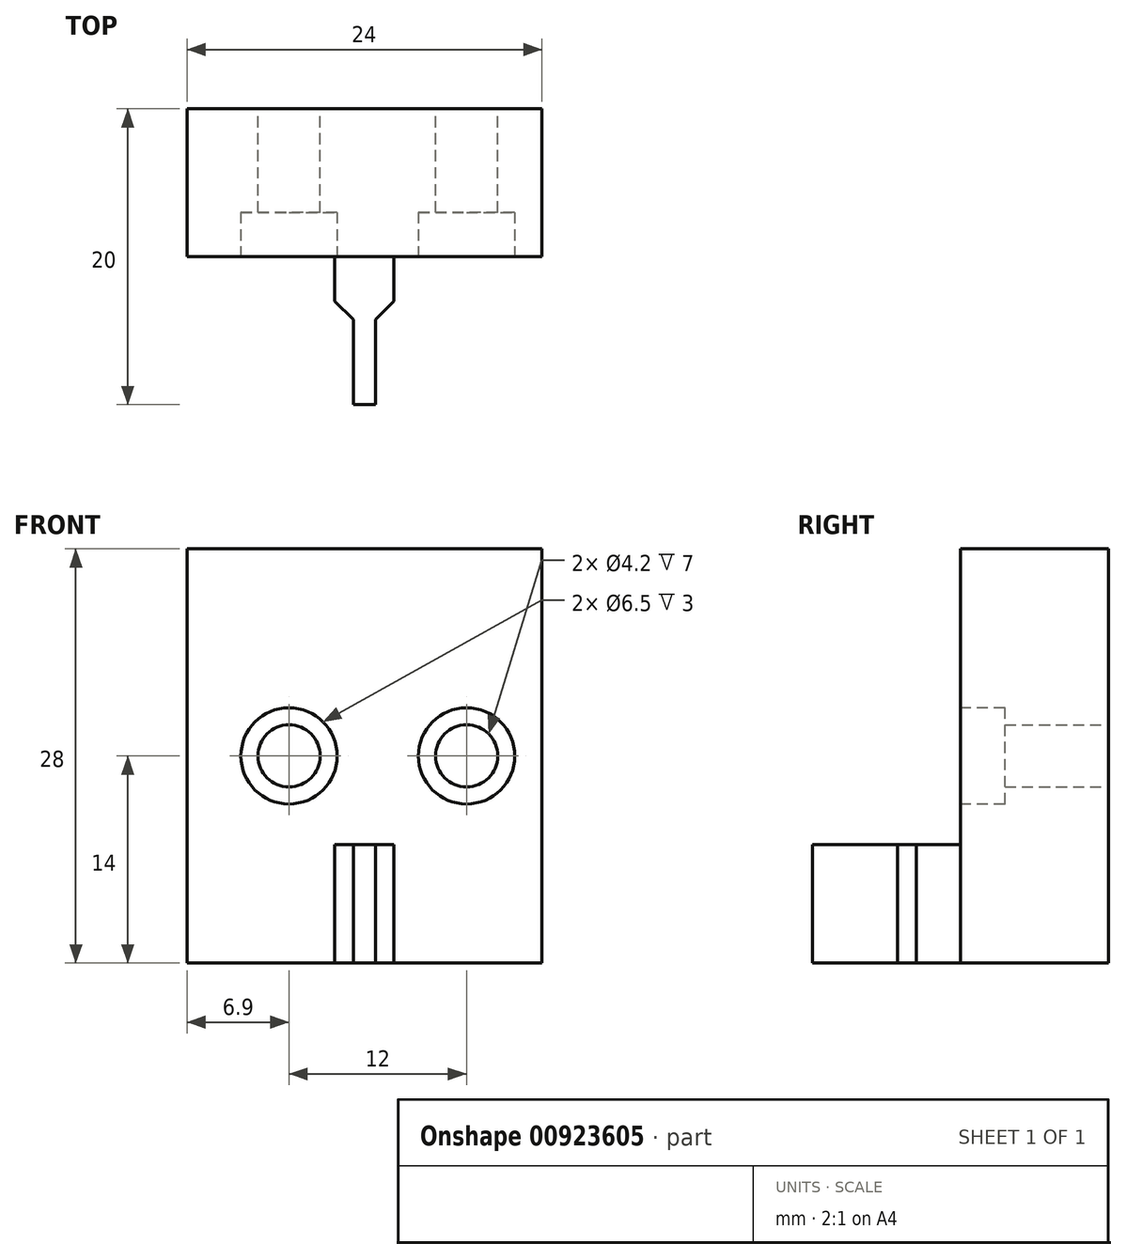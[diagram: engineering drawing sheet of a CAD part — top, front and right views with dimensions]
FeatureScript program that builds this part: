
annotation { "Feature Type Name" : "Feature", "Feature Type Description" : "" }
export const myFeature = defineFeature(function(context is Context, id is Id, definition is map)
    precondition{}
    {
        {
            var Q0;
            Q0=qCreatedBy(makeId("Front.planeOp"),FACE);
            var sketch = newSketch(context, id + "F0", { "sketchPlane" : qUnion([Q0])});
            skLineSegment(sketch, "E0.bottom", {"start": v(-12, -14) * mm, "end": v(12, -14) * mm});
            skLineSegment(sketch, "E0.top", {"start": v(-12, 14) * mm, "end": v(12, 14) * mm});
            skLineSegment(sketch, "E0.left", {"start": v(-12, -14) * mm, "end": v(-12, 14) * mm});
            skLineSegment(sketch, "E0.right", {"start": v(12, -14) * mm, "end": v(12, 14) * mm});
            skPoint(sketch, "E0.middle", {"position": v(0, 0) * mm});
            skCircle(sketch, "E1", {"center": v(6.9, 0) * mm, "radius": 2.1 * mm});
            skCircle(sketch, "E2", {"center": v(-5.1, 0) * mm, "radius": 2.1 * mm});
            skSolve(sketch);
        }
        {
            var Q0;
            Q0=makeQuery(id+"F0.imprint","IMPRINT",FACE,{"disambiguationData":[TD([[makeQuery(id+"F0.imprint","IMPRINT",EDGE,{"derivedFrom":sQuery(id+"F0.wireOp",EDGE,"E0.bottom")}),1.0]])]});
            extrude(context, id + "F1", {"entities" : qUnion([Q0]), "depth" : 10 * mm, "offsetDistance" : 25 * mm});
        }
        {
            var Q0;
            Q0=makeQuery(id+"F1.opExtrude","CAP_FACE",FACE,{"disambiguationData":[OSD([sQuery(id+"F0.wireOp",EDGE,"E0.bottom"),sQuery(id+"F0.wireOp",EDGE,"E0.top"),sQuery(id+"F0.wireOp",EDGE,"E0.left"),sQuery(id+"F0.wireOp",EDGE,"E0.right"),sQuery(id+"F0.wireOp",EDGE,"E1"),sQuery(id+"F0.wireOp",EDGE,"E2")])],"isStart":false});
            var sketch = newSketch(context, id + "F2", { "sketchPlane" : qUnion([Q0])});
            skLineSegment(sketch, "E3.top", {"start": v(2, -6) * mm, "end": v(-2, -6) * mm});
            skLineSegment(sketch, "E3.left", {"start": v(2, -14) * mm, "end": v(2, -6) * mm});
            skLineSegment(sketch, "E3.right", {"start": v(-2, -14) * mm, "end": v(-2, -6) * mm});
            skPoint(sketch, "E3.middle", {"position": v(0, 0) * mm});
            skLineSegment(sketch, "E4", {"start": v(-2, -14) * mm, "end": v(2, -14) * mm});
            skSolve(sketch);
        }
        {
            var Q0;
            Q0 = qSketchRegion(id + "F2", true);
            extrude(context, id + "F3", {"entities" : qUnion([Q0]), "operationType" : NewBodyOperationType.ADD, "depth" : 5 * mm, "offsetDistance" : 25 * mm});
        }
        {
            var Q0;
            Q0=makeQuery(id+"F3.opExtrude","CAP_FACE",FACE,{"disambiguationData":[OSD([sQuery(id+"F2.wireOp",EDGE,"E3.top"),sQuery(id+"F2.wireOp",EDGE,"E3.left"),sQuery(id+"F2.wireOp",EDGE,"E3.right"),sQuery(id+"F2.wireOp",EDGE,"E4")])],"isStart":false});
            var sketch = newSketch(context, id + "F4", { "sketchPlane" : qUnion([Q0])});
            skLineSegment(sketch, "E5.bottom", {"start": v(-0.75, -6) * mm, "end": v(0.75, -6) * mm});
            skLineSegment(sketch, "E5.top", {"start": v(-0.75, -14) * mm, "end": v(0.75, -14) * mm});
            skLineSegment(sketch, "E5.left", {"start": v(-0.75, -6) * mm, "end": v(-0.75, -14) * mm});
            skLineSegment(sketch, "E5.right", {"start": v(0.75, -6) * mm, "end": v(0.75, -14) * mm});
            skPoint(sketch, "E5.middle", {"position": v(0, 0) * mm});
            skSolve(sketch);
        }
        {
            var Q0;
            Q0 = qSketchRegion(id + "F4", true);
            extrude(context, id + "F5", {"entities" : qUnion([Q0]), "operationType" : NewBodyOperationType.ADD, "depth" : 5 * mm, "offsetDistance" : 25 * mm});
        }
        {
            var Q0;
            Q0=makeQuery(id+"F3.opExtrude","CAP_EDGE",EDGE,{"disambiguationData":[OSD([sQuery(id+"F2.wireOp",EDGE,"E3.left")])],"isStart":false});
            var Q1;
            Q1=makeQuery(id+"F3.opExtrude","CAP_EDGE",EDGE,{"disambiguationData":[OSD([sQuery(id+"F2.wireOp",EDGE,"E3.right")])],"isStart":false});
            chamfer(context, id + "F6", {"entities" : qUnion([Q0, Q1]), "width" : 2 * mm, "tangentPropagation" : true});
        }
        {
            var Q0;
            Q0=makeQuery(id+"F1.opExtrude","CAP_FACE",FACE,{"disambiguationData":[OSD([sQuery(id+"F0.wireOp",EDGE,"E0.bottom"),sQuery(id+"F0.wireOp",EDGE,"E0.top"),sQuery(id+"F0.wireOp",EDGE,"E0.left"),sQuery(id+"F0.wireOp",EDGE,"E0.right"),sQuery(id+"F0.wireOp",EDGE,"E1"),sQuery(id+"F0.wireOp",EDGE,"E2")])],"isStart":false});
            var sketch = newSketch(context, id + "F7", { "sketchPlane" : qUnion([Q0])});
            skCircle(sketch, "E6", {"center": v(-5.1, 0) * mm, "radius": 3.25 * mm});
            skCircle(sketch, "E7", {"center": v(6.9, 0) * mm, "radius": 3.25 * mm});
            skSolve(sketch);
        }
        {
            var Q0;
            Q0 = qSketchRegion(id + "F7", true);
            extrude(context, id + "F8", {"entities" : qUnion([Q0]), "operationType" : NewBodyOperationType.REMOVE, "oppositeDirection" : true, "depth" : 3 * mm, "offsetDistance" : 25 * mm});
        }
    });
